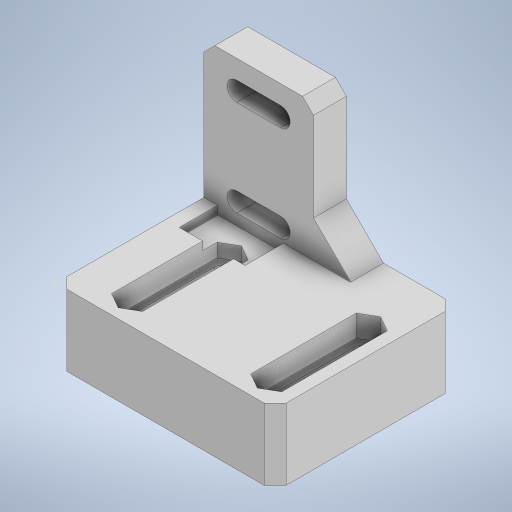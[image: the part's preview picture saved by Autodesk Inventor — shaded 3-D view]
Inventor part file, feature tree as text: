
AUTODESK INVENTOR PART (.ipt)
format: ipt  version: 2024 (Build 280153020, 153B)  size: 350,208 bytes
history: native  units: in
note: dims shown in document units (in); Inventor stores cm internally (conversion verified against a paired STEP export)
features: sketch x8, extrude x7, chamfer x4
ambient origin geometry x8: Origin, YZ Plane, XZ Plane, XY Plane, X Axis, Y Axis, Z Axis, Center Point
bodies: Solid1 (feature_tree)
feature tree (19):
  extrude  "Extrusion1"  Depth=1.063in
  extrude  "Extrusion2"  Depth=0.2362in
  extrude  "Extrusion3"  Depth=1.5748in TaperAngle=0.0deg
  sketch  "Sketch4"  dims[d8=0.1969in d9=0.1969in]
  extrude  "Extrusion4"  Depth=0.1969in
  extrude  "Extrusion5"  Depth=1.0in
  extrude  "Extrusion6"  Depth=1.0in
  chamfer  "Chamfer1"  Distance=1.5748in
  chamfer  "Chamfer2"  Distance=0.111in
  chamfer  "Chamfer3"  Distance=0.111in
  chamfer  "Chamfer4"  Distance=0.1575in
  extrude  "Extrusion7"  Depth=0.0591in
  sketch  "Sketch1"  dims[d0=0.5118in d1=1.063in]
  sketch  "Sketch2"  dims[d2=1.5748in d3=0.0in d4=0.2362in]
  sketch  "Sketch3"  dims[d5=1.4961in d6=1.5748in d7=0.0in]
  sketch  "Sketch5"  dims[d10=0.6299in d11=1.0in]
  sketch  "Sketch6"  dims[d12=0.1299in d13=0.1969in d14=0.6299in d15=1.0in d16=0.1299in d17=1.5748in d18=0.0in]
  sketch  "Sketch7"  dims[d19=0.111in]
  sketch  "Sketch8"  dims[d20=0.111in d21=0.111in d23=0.111in d24=0.111in d25=0.111in d26=0.1575in d27=0.0in d28=0.0906in d29=0.689in d30=0.2362in d31=0.315in d32=0.315in d33=0.1378in d34=0.1378in d35=1.405in d36=0.0in d37=1.7825in d38=0.0in d39=0.2662in d40=0.0787in d41=45.0deg d42=0.0787in d43=0.0787in d44=45.0deg d45=0.0787in d46=0.0787in d47=45.0deg d48=0.0787in d49=0.0787in d50=45.0deg d53=0.0984in d54=0.4724in d55=0.2756in d56=0.0591in d57=0.0in]
